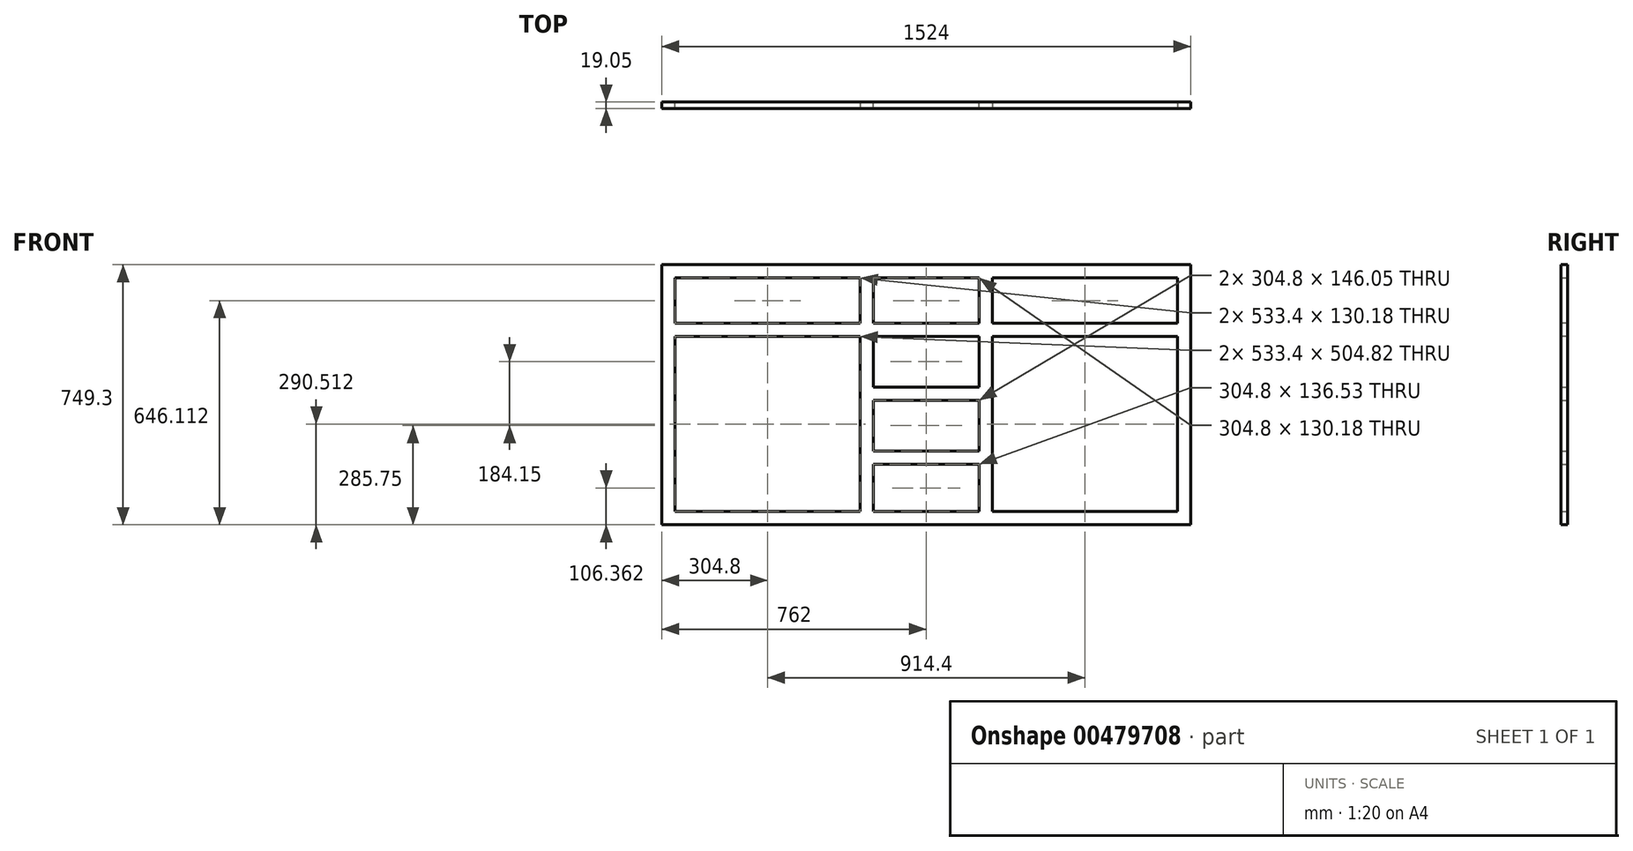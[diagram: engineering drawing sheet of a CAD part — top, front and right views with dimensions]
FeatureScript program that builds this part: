
annotation { "Feature Type Name" : "Feature", "Feature Type Description" : "" }
export const myFeature = defineFeature(function(context is Context, id is Id, definition is map)
    precondition{}
    {
        {
            var Q0;
            Q0=qCreatedBy(makeId("Front.planeOp"),FACE);
            var sketch = newSketch(context, id + "F0", { "sketchPlane" : qUnion([Q0])});
            skLineSegment(sketch, "E0.bottom", {"start": v(0, 0) * mm, "end": v(1524, 0) * mm});
            skLineSegment(sketch, "E0.top", {"start": v(0, 749.3) * mm, "end": v(1524, 749.3) * mm});
            skLineSegment(sketch, "E0.left", {"start": v(0, 0) * mm, "end": v(0, 749.3) * mm});
            skLineSegment(sketch, "E0.right", {"start": v(1524, 0) * mm, "end": v(1524, 749.3) * mm});
            skLineSegment(sketch, "E1.0", {"start": v(38.1, 711.2) * mm, "end": v(571.5, 711.2) * mm});
            skLineSegment(sketch, "E1.1", {"start": v(38.1, 38.1) * mm, "end": v(38.1, 711.2) * mm});
            skLineSegment(sketch, "E1.2", {"start": v(38.1, 38.1) * mm, "end": v(571.5, 38.1) * mm});
            skLineSegment(sketch, "E1.3", {"start": v(1485.9, 38.1) * mm, "end": v(1485.9, 711.2) * mm});
            skLineSegment(sketch, "E2", {"start": v(571.5, 711.2) * mm, "end": v(571.5, 38.1) * mm});
            skLineSegment(sketch, "E3", {"start": v(609.6, 711.2) * mm, "end": v(609.6, 38.1) * mm});
            skLineSegment(sketch, "E4", {"start": v(914.4, 711.2) * mm, "end": v(914.4, 38.1) * mm});
            skLineSegment(sketch, "E5", {"start": v(952.5, 711.2) * mm, "end": v(952.5, 38.1) * mm});
            skLineSegment(sketch, "E6", {"start": v(38.1, 374.65) * mm, "end": v(571.5, 374.65) * mm, "construction": true});
            skLineSegment(sketch, "E7", {"start": v(952.5, 374.65) * mm, "end": v(1485.9, 374.65) * mm, "construction": true});
            skLineSegment(sketch, "E8.trimOffspring", {"start": v(609.6, 38.1) * mm, "end": v(914.4, 38.1) * mm});
            skLineSegment(sketch, "E9.trimOffspring", {"start": v(952.5, 38.1) * mm, "end": v(1485.9, 38.1) * mm});
            skLineSegment(sketch, "E10.trimOffspring", {"start": v(609.6, 711.2) * mm, "end": v(914.4, 711.2) * mm});
            skLineSegment(sketch, "E11.trimOffspring", {"start": v(952.5, 711.2) * mm, "end": v(1485.9, 711.2) * mm});
            skSolve(sketch);
        }
        {
            var Q0;
            Q0=makeQuery(id+"F0.imprint","IMPRINT",FACE,{"disambiguationData":[TD([[makeQuery(id+"F0.imprint","IMPRINT",EDGE,{"derivedFrom":sQuery(id+"F0.wireOp",EDGE,"E0.bottom")}),1.0]])]});
            extrude(context, id + "F1", {"entities" : qUnion([Q0]), "depth" : 19.05 * mm});
        }
        {
            var Q0;
            Q0=makeQuery(id+"F1.opExtrude","SWEPT_FACE",FACE,{"disambiguationData":[OSD([sQuery(id+"F0.wireOp",EDGE,"E1.1")])]});
            var sketch = newSketch(context, id + "F2", { "sketchPlane" : qUnion([Q0])});
            skLineSegment(sketch, "E12.bottom", {"start": v(-19.05, 581.02) * mm, "end": v(0, 581.02) * mm});
            skLineSegment(sketch, "E12.top", {"start": v(-19.05, 542.92) * mm, "end": v(0, 542.92) * mm});
            skLineSegment(sketch, "E12.left", {"start": v(-19.05, 581.02) * mm, "end": v(-19.05, 542.92) * mm});
            skLineSegment(sketch, "E12.right", {"start": v(0, 581.02) * mm, "end": v(0, 542.92) * mm});
            skSolve(sketch);
        }
        {
            var Q0;
            Q0=qSketchRegion(id+"F2",true);
            var Q1;
            Q1=makeQuery(id+"F1.opExtrude","SWEPT_FACE",FACE,{"disambiguationData":[OSD([sQuery(id+"F0.wireOp",EDGE,"E1.3")])]});
            extrude(context, id + "F3", {"entities" : qUnion([Q0]), "operationType" : NewBodyOperationType.ADD, "endBound" : BoundingType.UP_TO_SURFACE, "endBoundEntityFace" : qUnion([Q1]), "depth" : 25.4 * mm});
        }
        {
            var Q0;
            {var subQ3=sQuery(id+"F0.wireOp",EDGE,"E8.trimOffspring");var subQ6=sQuery(id+"F0.wireOp",EDGE,"E3");Q0=makeQuery(id+"F3.boolean.opBoolean","SPLIT",FACE,{"disambiguationData":[TD([makeQuery(id+"F1.opExtrude","SWEPT_FACE",FACE,{"disambiguationData":[OSD([subQ3])]})])],"derivedFrom":makeQuery(id+"F1.opExtrude","SWEPT_FACE",FACE,{"disambiguationData":[OSD([subQ6])]})});}
            var sketch = newSketch(context, id + "F4", { "sketchPlane" : qUnion([Q0])});
            skLineSegment(sketch, "E13.bottom", {"start": v(-19.05, 396.87) * mm, "end": v(0, 396.87) * mm});
            skLineSegment(sketch, "E13.top", {"start": v(-19.05, 358.77) * mm, "end": v(0, 358.77) * mm});
            skLineSegment(sketch, "E13.left", {"start": v(-19.05, 396.87) * mm, "end": v(-19.05, 358.77) * mm});
            skLineSegment(sketch, "E13.right", {"start": v(0, 396.87) * mm, "end": v(0, 358.77) * mm});
            skSolve(sketch);
        }
        {
            var Q0;
            Q0=qSketchRegion(id+"F4",true);
            extrude(context, id + "F5", {"entities" : qUnion([Q0]), "operationType" : NewBodyOperationType.ADD, "endBound" : BoundingType.UP_TO_NEXT, "depth" : 25.4 * mm});
        }
        {
            var Q0;
            {var subQ4=sQuery(id+"F0.wireOp",EDGE,"E8.trimOffspring");var subQ7=sQuery(id+"F0.wireOp",EDGE,"E3");var subQ18=makeQuery(id+"F1.opExtrude","SWEPT_FACE",FACE,{"disambiguationData":[OSD([subQ4])]});Q0=makeQuery(id+"F5.boolean.opBoolean","SPLIT",FACE,{"disambiguationData":[TD([subQ18])],"derivedFrom":makeQuery(id+"F3.boolean.opBoolean","SPLIT",FACE,{"disambiguationData":[TD([subQ18])],"derivedFrom":makeQuery(id+"F1.opExtrude","SWEPT_FACE",FACE,{"disambiguationData":[OSD([subQ7])]})})});}
            var sketch = newSketch(context, id + "F6", { "sketchPlane" : qUnion([Q0])});
            skLineSegment(sketch, "E14.bottom", {"start": v(-19.05, 212.72) * mm, "end": v(0, 212.72) * mm});
            skLineSegment(sketch, "E14.top", {"start": v(-19.05, 174.62) * mm, "end": v(0, 174.62) * mm});
            skLineSegment(sketch, "E14.left", {"start": v(-19.05, 212.72) * mm, "end": v(-19.05, 174.62) * mm});
            skLineSegment(sketch, "E14.right", {"start": v(0, 212.72) * mm, "end": v(0, 174.62) * mm});
            skSolve(sketch);
        }
        {
            var Q0;
            Q0=qSketchRegion(id+"F6",true);
            extrude(context, id + "F7", {"entities" : qUnion([Q0]), "operationType" : NewBodyOperationType.ADD, "endBound" : BoundingType.UP_TO_NEXT, "depth" : 25.4 * mm});
        }
    });
